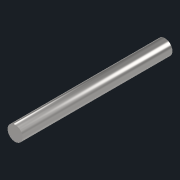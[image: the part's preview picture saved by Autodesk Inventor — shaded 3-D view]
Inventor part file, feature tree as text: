
AUTODESK INVENTOR PART (.ipt)
format: ipt  version: 2022.2 (Build 262287010, 287A)  size: 82,944 bytes
history: native  units: mm
features: extrude x1, sketch x1
ambient origin geometry x8: Origin, YZ Plane, XZ Plane, XY Plane, X Axis, Y Axis, Z Axis, Center Point
bodies: Solid1 (feature_tree)
feature tree (2):
  extrude  "Extrusion1"  Depth=50.0mm TaperAngle=0.0deg
  sketch  "Sketch1"  dims[d0=5.0mm d1=50.0mm d2=0.0mm]
